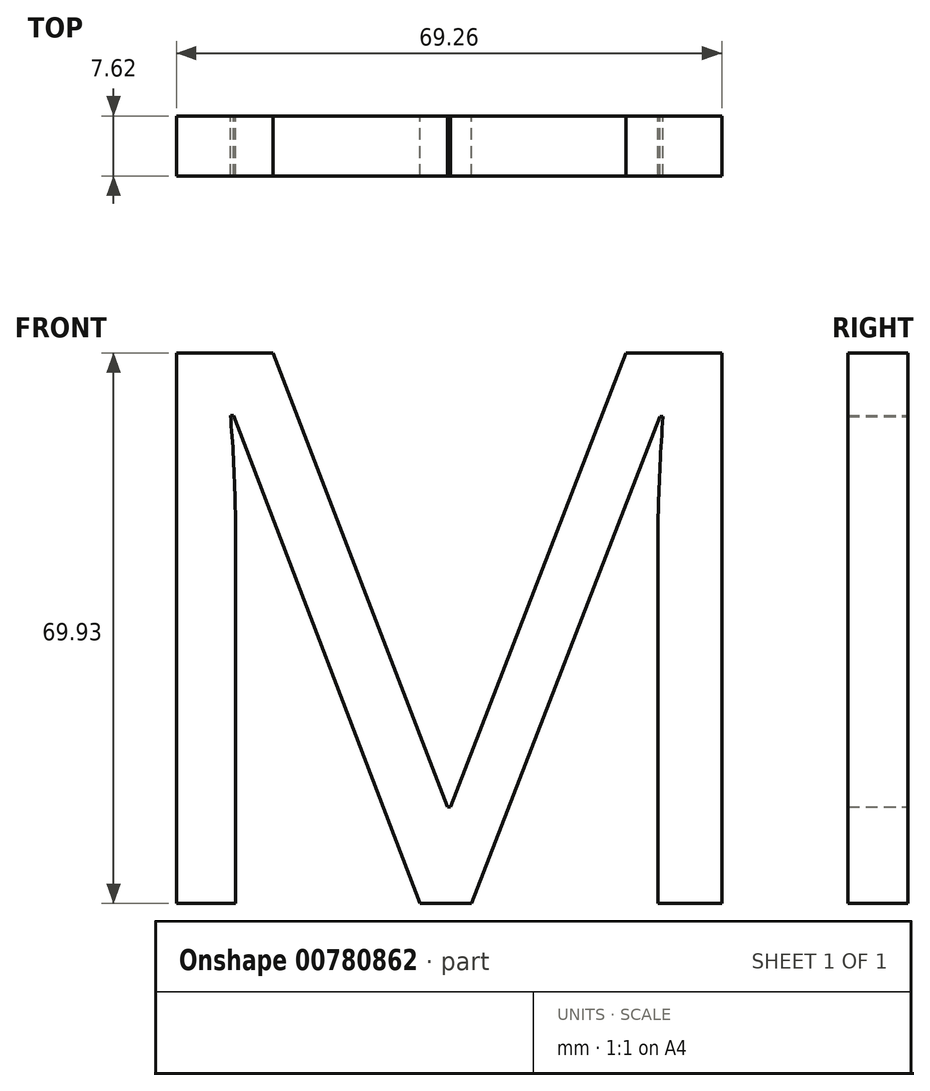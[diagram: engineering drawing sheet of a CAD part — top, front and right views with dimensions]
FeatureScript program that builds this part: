
annotation { "Feature Type Name" : "Feature", "Feature Type Description" : "" }
export const myFeature = defineFeature(function(context is Context, id is Id, definition is map)
    precondition{}
    {
        {
            var Q0;
            Q0=qCreatedBy(makeId("Front.planeOp"),FACE);
            var sketch = newSketch(context, id + "F0", { "sketchPlane" : qUnion([Q0])});
            skText(sketch, "E0", { "text": "M\n", "fontName": "OpenSans-Regular.ttf"});
            const initialGuessF0  = {"E0": [-0.06898, -0.03432, 1, 0, 0.07053]};
            skSetInitialGuess(sketch, initialGuessF0);
            skSolve(sketch);
        }
        {
            var Q0;
            Q0=makeQuery(id+"F0.imprint","IMPRINT",FACE,{"disambiguationData":[TD([[makeQuery(id+"F0.imprint","IMPRINT",EDGE,{"derivedFrom":sQuery(id+"F0.wireOp",EDGE,"E0.sketch_text.stroke-0")}),-1.0]])]});
            extrude(context, id + "F1", {"entities" : qUnion([Q0]), "depth" : 7.62 * mm, "offsetDistance" : 25.4 * mm});
        }
    });
